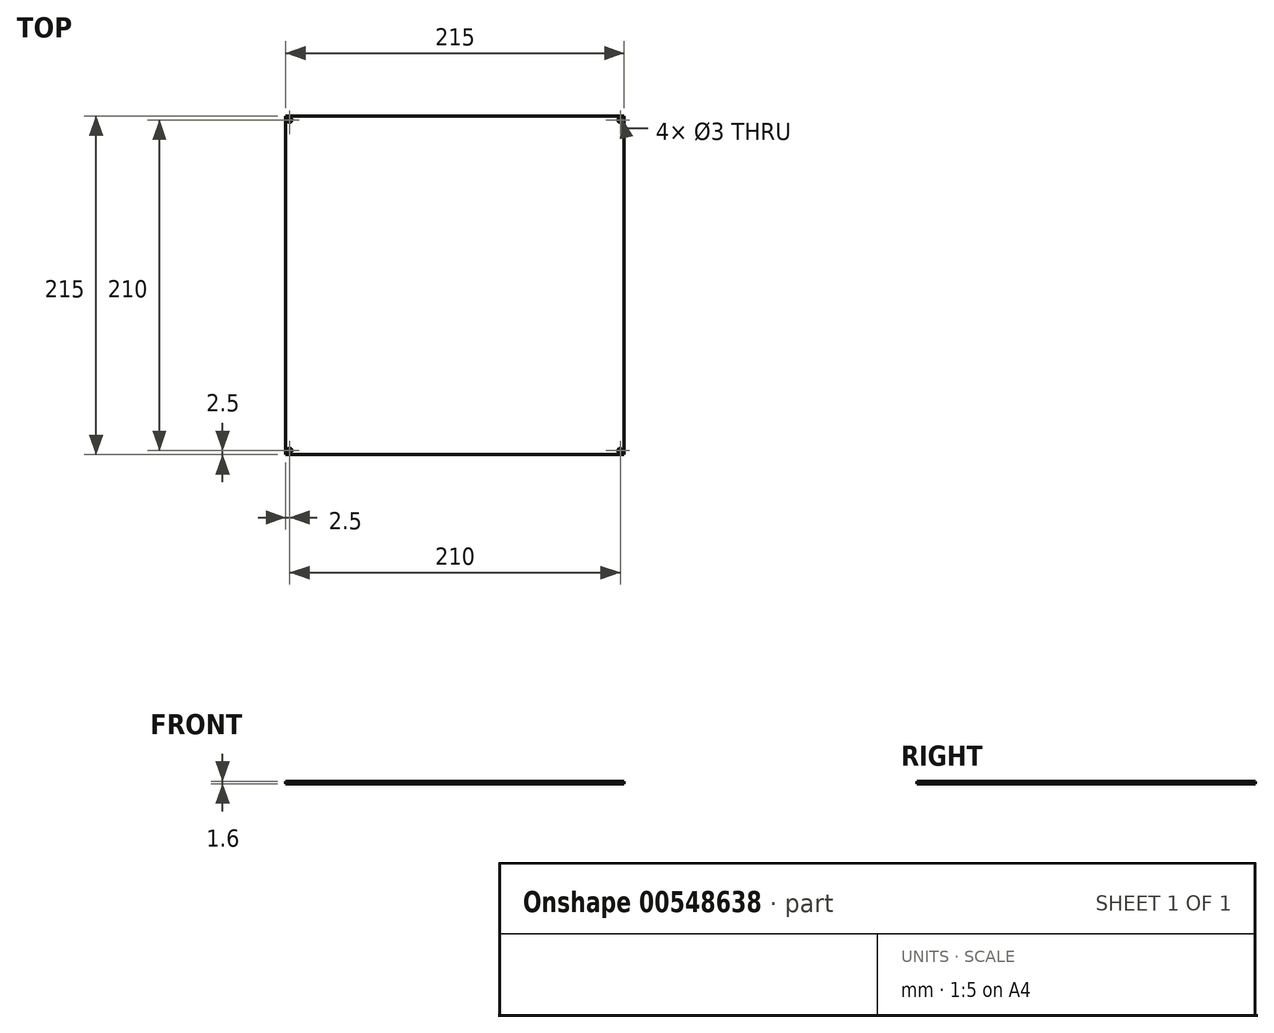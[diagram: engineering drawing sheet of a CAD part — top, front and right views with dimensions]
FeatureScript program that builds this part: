
annotation { "Feature Type Name" : "Feature", "Feature Type Description" : "" }
export const myFeature = defineFeature(function(context is Context, id is Id, definition is map)
    precondition{}
    {
        {
            var Q0;
            Q0=qCreatedBy(makeId("Top.planeOp"),FACE);
            var sketch = newSketch(context, id + "F0", { "sketchPlane" : qUnion([Q0])});
            skLineSegment(sketch, "E0.bottom", {"start": v(-107.5, 107.5) * mm, "end": v(107.5, 107.5) * mm});
            skLineSegment(sketch, "E0.top", {"start": v(-107.5, -107.5) * mm, "end": v(107.5, -107.5) * mm});
            skLineSegment(sketch, "E0.left", {"start": v(-107.5, 107.5) * mm, "end": v(-107.5, -107.5) * mm});
            skLineSegment(sketch, "E0.right", {"start": v(107.5, 107.5) * mm, "end": v(107.5, -107.5) * mm});
            skCircle(sketch, "E1", {"center": v(-105, 105) * mm, "radius": 1.5 * mm});
            skCircle(sketch, "E2.MirrorC", {"center": v(105, 105) * mm, "radius": 1.5 * mm});
            skCircle(sketch, "E3.MirrorC", {"center": v(-105, -105) * mm, "radius": 1.5 * mm});
            skCircle(sketch, "E4.MirrorC", {"center": v(105, -105) * mm, "radius": 1.5 * mm});
            skSolve(sketch);
        }
        {
            var Q0;
            Q0 = qSketchRegion(id + "F0", true);
            extrude(context, id + "F1", {"entities" : qUnion([Q0]), "flatOperationType" : FlatOperationType.REMOVE, "depth" : 1.6 * mm, "offsetDistance" : 25 * mm, "domain" : OperationDomain.MODEL});
        }
    });
